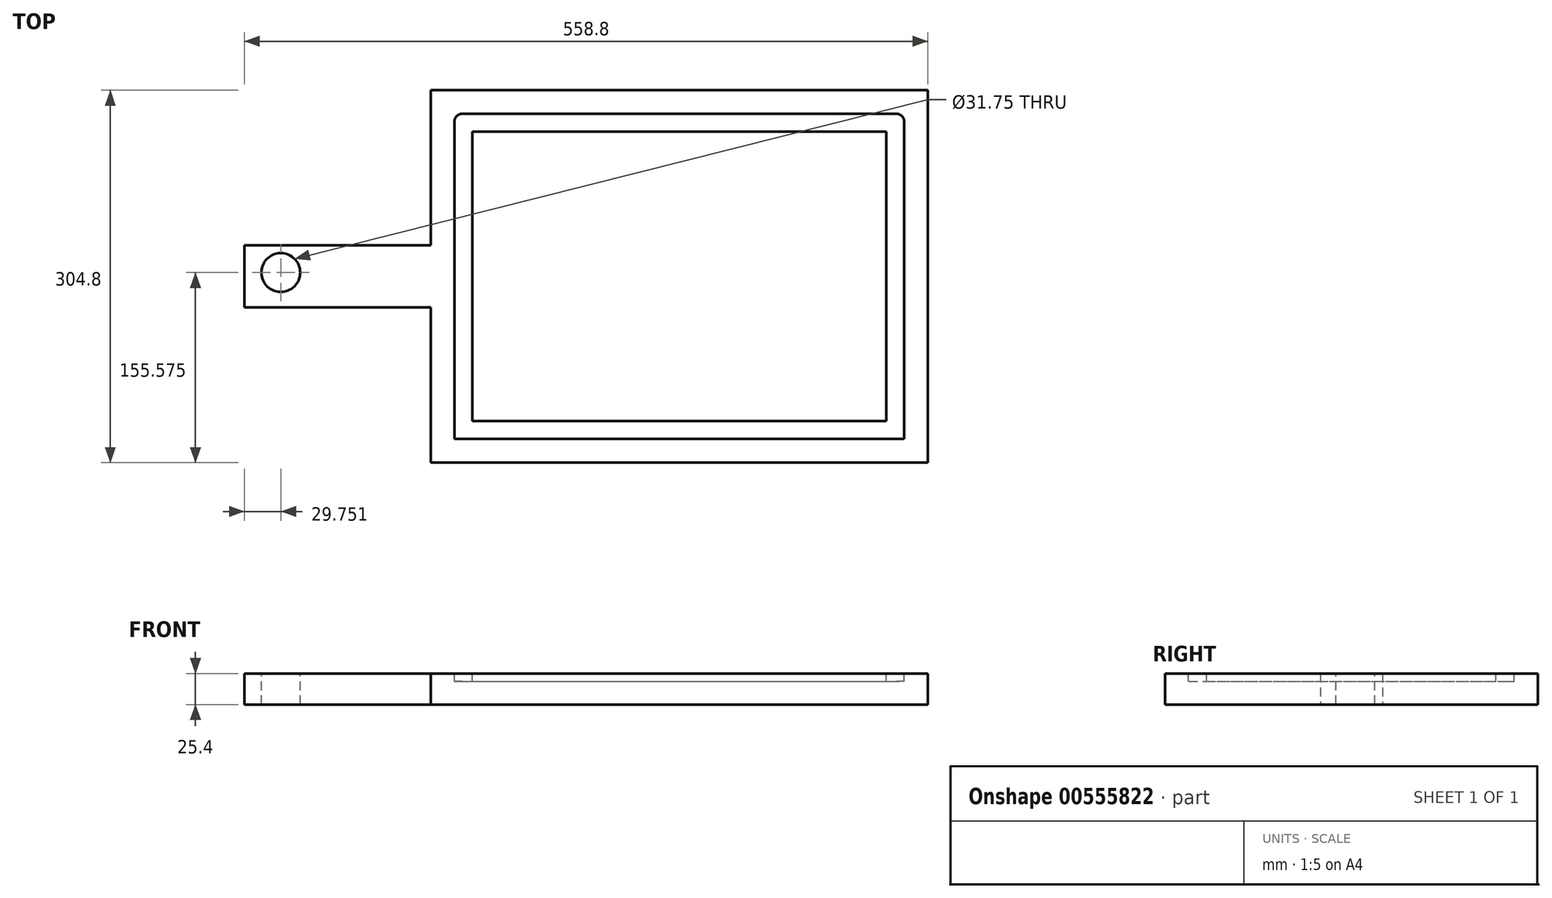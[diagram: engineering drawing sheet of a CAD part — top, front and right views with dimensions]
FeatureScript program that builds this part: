
annotation { "Feature Type Name" : "Feature", "Feature Type Description" : "" }
export const myFeature = defineFeature(function(context is Context, id is Id, definition is map)
    precondition{}
    {
        {
            var Q0;
            Q0=qCreatedBy(makeId("Top.planeOp"),FACE);
            var sketch = newSketch(context, id + "F0", { "sketchPlane" : qUnion([Q0])});
            skLineSegment(sketch, "E0.bottom", {"start": v(0, 0) * mm, "end": v(406.4, 0) * mm});
            skLineSegment(sketch, "E0.top", {"start": v(0, 304.8) * mm, "end": v(406.4, 304.8) * mm});
            skLineSegment(sketch, "E0.left", {"start": v(0, 0) * mm, "end": v(0, 304.8) * mm});
            skLineSegment(sketch, "E0.right", {"start": v(406.4, 0) * mm, "end": v(406.4, 304.8) * mm});
            skLineSegment(sketch, "E1.bottom", {"start": v(0, 127) * mm, "end": v(-152.4, 127) * mm});
            skLineSegment(sketch, "E1.top", {"start": v(0, 177.8) * mm, "end": v(-152.4, 177.8) * mm});
            skLineSegment(sketch, "E1.left", {"start": v(0, 127) * mm, "end": v(0, 177.8) * mm});
            skLineSegment(sketch, "E1.right", {"start": v(-152.4, 127) * mm, "end": v(-152.4, 177.8) * mm});
            skSolve(sketch);
        }
        {
            var Q0;
            {var subQ3=sQuery(id+"F0.wireOp",EDGE,"E0.bottom");Q0=makeQuery(id+"F0.imprint","IMPRINT",FACE,{"disambiguationData":[TD([[makeQuery(id+"F0.imprint","IMPRINT",EDGE,{"derivedFrom":subQ3}),1.0]])]});}
            var Q1;
            Q1=makeQuery(id+"F0.imprint","IMPRINT",FACE,{"disambiguationData":[TD([[makeQuery(id+"F0.imprint","IMPRINT",EDGE,{"derivedFrom":sQuery(id+"F0.wireOp",EDGE,"E1.bottom")}),-1.0]])]});
            extrude(context, id + "F1", {"entities" : qUnion([Q0, Q1]), "depth" : 25.4 * mm, "offsetDistance" : 25.4 * mm});
        }
        {
            var Q0;
            Q0=makeQuery(id+"F1.opExtrude","CAP_FACE",FACE,{"disambiguationData":[OSD([sQuery(id+"F0.wireOp",EDGE,"E0.bottom"),sQuery(id+"F0.wireOp",EDGE,"E0.top"),sQuery(id+"F0.wireOp",EDGE,"E0.left"),sQuery(id+"F0.wireOp",EDGE,"E0.right"),sQuery(id+"F0.wireOp",EDGE,"E1.bottom"),sQuery(id+"F0.wireOp",EDGE,"E1.top"),sQuery(id+"F0.wireOp",EDGE,"E1.right")])],"isStart":false});
            var sketch = newSketch(context, id + "F2", { "sketchPlane" : qUnion([Q0])});
            skCircle(sketch, "E2", {"center": v(-122.65, 155.58) * mm, "radius": 15.87 * mm});
            skSolve(sketch);
        }
        {
            var Q0;
            Q0 = qSketchRegion(id + "F2", true);
            extrude(context, id + "F3", {"entities" : qUnion([Q0]), "operationType" : NewBodyOperationType.REMOVE, "oppositeDirection" : true, "depth" : 25.4 * mm, "offsetDistance" : 25.4 * mm});
        }
        {
            var Q0;
            Q0=makeQuery(id+"F1.opExtrude","CAP_FACE",FACE,{"disambiguationData":[OSD([sQuery(id+"F0.wireOp",EDGE,"E0.bottom"),sQuery(id+"F0.wireOp",EDGE,"E0.top"),sQuery(id+"F0.wireOp",EDGE,"E0.left"),sQuery(id+"F0.wireOp",EDGE,"E0.right"),sQuery(id+"F0.wireOp",EDGE,"E1.bottom"),sQuery(id+"F0.wireOp",EDGE,"E1.top"),sQuery(id+"F0.wireOp",EDGE,"E1.right")])],"isStart":false});
            var sketch = newSketch(context, id + "F4", { "sketchPlane" : qUnion([Q0])});
            skLineSegment(sketch, "E3.0", {"start": v(19.3, 19.3) * mm, "end": v(19.3, 127) * mm});
            skLineSegment(sketch, "E3.1", {"start": v(19.3, 177.8) * mm, "end": v(19.3, 285.5) * mm});
            skLineSegment(sketch, "E3.2", {"start": v(19.3, 285.5) * mm, "end": v(387.1, 285.5) * mm});
            skLineSegment(sketch, "E3.3", {"start": v(387.1, 19.3) * mm, "end": v(387.1, 285.5) * mm});
            skLineSegment(sketch, "E3.4", {"start": v(19.3, 19.3) * mm, "end": v(387.1, 19.3) * mm});
            skLineSegment(sketch, "E4", {"start": v(19.3, 177.8) * mm, "end": v(19.3, 127) * mm});
            skLineSegment(sketch, "E5.0", {"start": v(34.04, 177.8) * mm, "end": v(34.04, 270.76) * mm});
            skLineSegment(sketch, "E5.1", {"start": v(372.36, 34.04) * mm, "end": v(372.36, 270.76) * mm});
            skLineSegment(sketch, "E5.2", {"start": v(34.04, 34.04) * mm, "end": v(372.36, 34.04) * mm});
            skLineSegment(sketch, "E5.3", {"start": v(34.04, 270.76) * mm, "end": v(372.36, 270.76) * mm});
            skLineSegment(sketch, "E5.4", {"start": v(34.04, 34.04) * mm, "end": v(34.04, 127) * mm});
            skLineSegment(sketch, "E5.5", {"start": v(34.04, 177.8) * mm, "end": v(34.04, 127) * mm});
            skSolve(sketch);
        }
        {
            var Q0;
            Q0=makeQuery(id+"F4.imprint","IMPRINT",FACE,{"disambiguationData":[TD([[makeQuery(id+"F4.imprint","IMPRINT",EDGE,{"derivedFrom":sQuery(id+"F4.wireOp",EDGE,"E3.0")}),-1.0]])]});
            extrude(context, id + "F5", {"entities" : qUnion([Q0]), "operationType" : NewBodyOperationType.REMOVE, "oppositeDirection" : true, "depth" : 6.35 * mm, "offsetDistance" : 25.4 * mm});
        }
        {
            var Q0;
            Q0=makeQuery(id+"F5.boolean.opBoolean","COPY",EDGE,{"derivedFrom":makeQuery(id+"F5.opExtrude","SWEPT_EDGE",EDGE,{"disambiguationData":[OSD([sQuery(id+"F4.wireOp",EDGE,"E3.1"),sQuery(id+"F4.wireOp",EDGE,"E3.2")])]})});
            var Q1;
            Q1=makeQuery(id+"F5.boolean.opBoolean","COPY",EDGE,{"derivedFrom":makeQuery(id+"F5.opExtrude","SWEPT_EDGE",EDGE,{"disambiguationData":[OSD([sQuery(id+"F4.wireOp",EDGE,"E3.2"),sQuery(id+"F4.wireOp",EDGE,"E3.3")])]})});
            fillet(context, id + "F6", {"entities" : qUnion([Q0, Q1]), "radius" : 6.35 * mm, "tangentPropagation" : true, "allowEdgeOverflow" : false});
        }
    });
